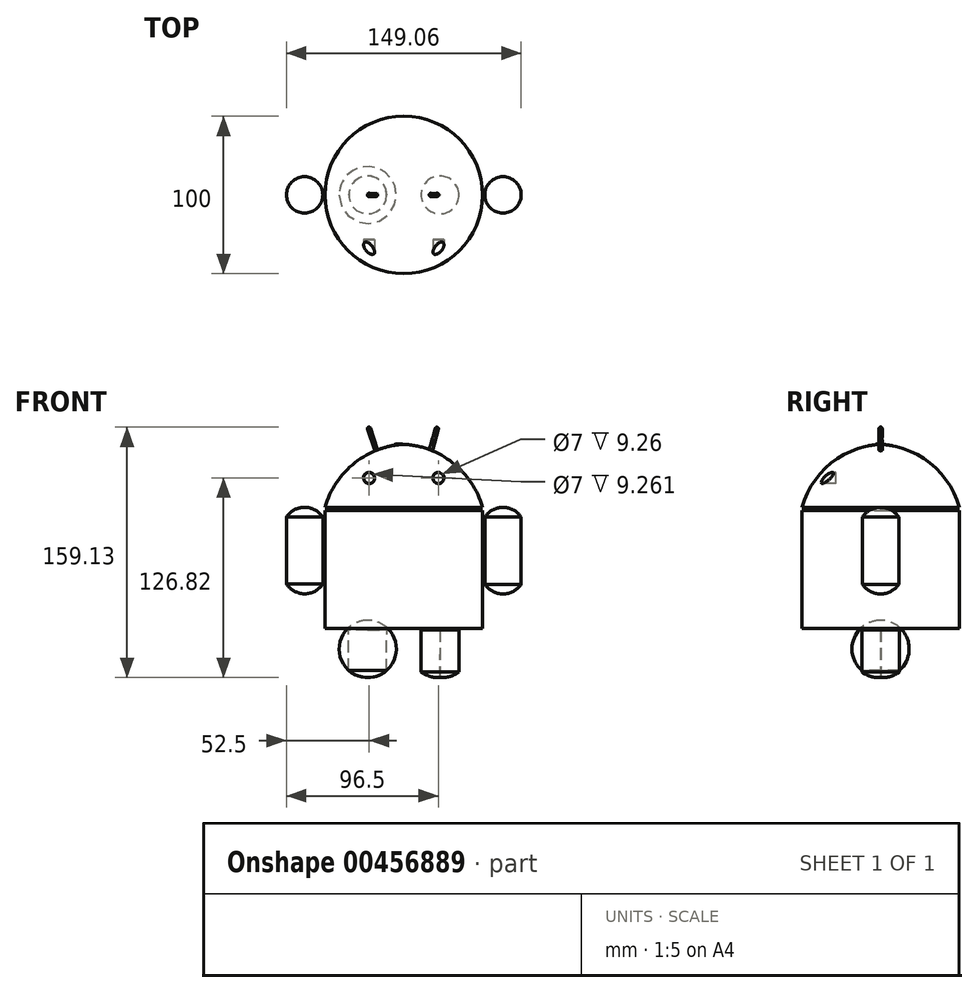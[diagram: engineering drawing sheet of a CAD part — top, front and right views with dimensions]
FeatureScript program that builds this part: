
annotation { "Feature Type Name" : "Feature", "Feature Type Description" : "" }
export const myFeature = defineFeature(function(context is Context, id is Id, definition is map)
    precondition{}
    {
        {
            var Q0;
            Q0=qCreatedBy(makeId("Front.planeOp"),FACE);
            var sketch = newSketch(context, id + "F0", { "sketchPlane" : qUnion([Q0])});
            skArc(sketch, "E0", {"start": v(0, 40) * mm, "mid": v(-31.42, 28.03) * mm, "end": v(-50, 0) * mm});
            skLineSegment(sketch, "E1", {"start": v(-50, 0) * mm, "end": v(0, 0) * mm});
            skLineSegment(sketch, "E2", {"start": v(0, 0) * mm, "end": v(0, 40) * mm});
            skSolve(sketch);
        }
        {
            var Q0;
            Q0=makeQuery(id+"F0.imprint","IMPRINT",FACE,{"disambiguationData":[TD([[makeQuery(id+"F0.imprint","IMPRINT",EDGE,{"derivedFrom":sQuery(id+"F0.wireOp",EDGE,"E0")}),1.0]])]});
            var Q1;
            Q1=sQuery(id+"F0.wireOp",EDGE,"E2");
            revolve(context, id + "F1", {"entities" : qUnion([Q0]), "axis" : qUnion([Q1]), "revolveType" : RevolveType.FULL});
        }
        {
            var Q0;
            Q0=qCreatedBy(makeId("Front.planeOp"),FACE);
            var sketch = newSketch(context, id + "F2", { "sketchPlane" : qUnion([Q0])});
            skLineSegment(sketch, "E3.bottom", {"start": v(0, -77) * mm, "end": v(-50, -77) * mm});
            skLineSegment(sketch, "E3.top", {"start": v(0, -2) * mm, "end": v(-50, -2) * mm});
            skLineSegment(sketch, "E3.left", {"start": v(0, -77) * mm, "end": v(0, -2) * mm});
            skLineSegment(sketch, "E3.right", {"start": v(-50, -77) * mm, "end": v(-50, -2) * mm});
            skSolve(sketch);
        }
        {
            var Q0;
            Q0=makeQuery(id+"F2.imprint","IMPRINT",FACE,{"disambiguationData":[TD([[makeQuery(id+"F2.imprint","IMPRINT",EDGE,{"derivedFrom":sQuery(id+"F2.wireOp",EDGE,"E3.bottom")}),-1.0]])]});
            var Q1;
            Q1=sQuery(id+"F2.wireOp",EDGE,"E3.left");
            revolve(context, id + "F3", {"entities" : qUnion([Q0]), "axis" : qUnion([Q1]), "revolveType" : RevolveType.FULL});
        }
        {
            var Q0;
            Q0=qCreatedBy(makeId("Front.planeOp"),FACE);
            cPlane(context, id + "F4", {"entities" : qUnion([Q0]), "cplaneType" : CPlaneType.OFFSET, "offset" : 38.5 * mm, "width" : 150 * mm, "height" : 150 * mm});
        }
        {
            var Q0;
            Q0=qCreatedBy(id+"F4.planeOp",FACE);
            var sketch = newSketch(context, id + "F5", { "sketchPlane" : qUnion([Q0])});
            skCircle(sketch, "E4", {"center": v(-22, 18.6) * mm, "radius": 3.5 * mm});
            skCircle(sketch, "E5", {"center": v(22, 18.6) * mm, "radius": 3.5 * mm});
            skSolve(sketch);
        }
        {
            var Q0;
            Q0 = qSketchRegion(id + "F5", true);
            extrude(context, id + "F6", {"entities" : qUnion([Q0]), "operationType" : NewBodyOperationType.REMOVE, "oppositeDirection" : true, "depth" : 10 * mm});
        }
        {
            var Q0;
            Q0=qCreatedBy(makeId("Front.planeOp"),FACE);
            var sketch = newSketch(context, id + "F7", { "sketchPlane" : qUnion([Q0])});
            skLineSegment(sketch, "E6", {"start": v(-15, 28.86) * mm, "end": v(-22.4, 50.82) * mm});
            skLineSegment(sketch, "E7", {"start": v(15, 29.08) * mm, "end": v(21.3, 50.82) * mm});
            skSolve(sketch);
        }
        {
            var Q0;
            Q0=qCreatedBy(makeId("Front.planeOp"),FACE);
            var sketch = newSketch(context, id + "F8", { "sketchPlane" : qUnion([Q0])});
            skArc(sketch, "E8", {"start": v(-22.43, 50.86) * mm, "mid": v(-23.02, 50.35) * mm, "end": v(-23.1, 49.57) * mm});
            skLineSegment(sketch, "E9", {"start": v(-23.1, 49.57) * mm, "end": v(-18.36, 35.82) * mm});
            skLineSegment(sketch, "E10", {"start": v(-18.36, 35.82) * mm, "end": v(-17.46, 36.13) * mm});
            skLineSegment(sketch, "E11", {"start": v(-17.46, 36.13) * mm, "end": v(-22.43, 50.86) * mm});
            skSolve(sketch);
        }
        {
            var Q0;
            Q0 = qSketchRegion(id + "F8", true);
            var Q1;
            Q1=sQuery(id+"F8.wireOp",EDGE,"E11");
            revolve(context, id + "F9", {"operationType" : NewBodyOperationType.ADD, "entities" : qUnion([Q0]), "axis" : qUnion([Q1]), "revolveType" : RevolveType.FULL});
        }
        {
            var Q0;
            Q0=qCreatedBy(makeId("Front.planeOp"),FACE);
            var sketch = newSketch(context, id + "F10", { "sketchPlane" : qUnion([Q0])});
            skArc(sketch, "E12", {"start": v(21.29, 50.83) * mm, "mid": v(20.67, 50.81) * mm, "end": v(20.16, 50.46) * mm});
            skLineSegment(sketch, "E13.0", {"start": v(14.04, 29.35) * mm, "end": v(20.16, 50.46) * mm});
            skLineSegment(sketch, "E14", {"start": v(14.04, 29.35) * mm, "end": v(15.08, 29.05) * mm});
            skLineSegment(sketch, "E15", {"start": v(15.08, 29.05) * mm, "end": v(21.29, 50.83) * mm});
            skSolve(sketch);
        }
        {
            var Q0;
            Q0=makeQuery(id+"F10.imprint","IMPRINT",FACE,{"disambiguationData":[TD([[makeQuery(id+"F10.imprint","IMPRINT",EDGE,{"derivedFrom":sQuery(id+"F10.wireOp",EDGE,"E12")}),1.0]])]});
            var Q1;
            Q1=sQuery(id+"F10.wireOp",EDGE,"E15");
            revolve(context, id + "F11", {"operationType" : NewBodyOperationType.ADD, "entities" : qUnion([Q0]), "axis" : qUnion([Q1]), "revolveType" : RevolveType.FULL});
        }
        {
            var Q0;
            Q0=qCreatedBy(makeId("Front.planeOp"),FACE);
            var sketch = newSketch(context, id + "F12", { "sketchPlane" : qUnion([Q0])});
            skArc(sketch, "E16", {"start": v(-62.96, 0) * mm, "mid": v(-69.5, -1.63) * mm, "end": v(-74.5, -6.15) * mm});
            skLineSegment(sketch, "E17", {"start": v(-74.5, -6.15) * mm, "end": v(-74.5, -48.81) * mm});
            skArc(sketch, "E18", {"start": v(-74.5, -48.81) * mm, "mid": v(-69.5, -53.33) * mm, "end": v(-62.96, -54.96) * mm});
            skLineSegment(sketch, "E19", {"start": v(-62.96, 0) * mm, "end": v(-62.96, -54.96) * mm});
            skLineSegment(sketch, "E20", {"start": v(-62.96, 0) * mm, "end": v(0, 0) * mm, "construction": true});
            skLineSegment(sketch, "E21", {"start": v(-62.96, -54.96) * mm, "end": v(0, 0) * mm, "construction": true});
            skSolve(sketch);
        }
        {
            var Q0;
            Q0=makeQuery(id+"F12.imprint","IMPRINT",FACE,{"disambiguationData":[TD([[makeQuery(id+"F12.imprint","IMPRINT",EDGE,{"derivedFrom":sQuery(id+"F12.wireOp",EDGE,"E16")}),1.0]])]});
            var Q1;
            Q1=sQuery(id+"F12.wireOp",EDGE,"E19");
            revolve(context, id + "F13", {"entities" : qUnion([Q0]), "axis" : qUnion([Q1]), "revolveType" : RevolveType.FULL});
        }
        {
            var Q0;
            Q0=qCreatedBy(makeId("Front.planeOp"),FACE);
            var sketch = newSketch(context, id + "F14", { "sketchPlane" : qUnion([Q0])});
            skArc(sketch, "E22", {"start": v(63.03, 0) * mm, "mid": v(56.47, -1.67) * mm, "end": v(51.49, -6.24) * mm});
            skLineSegment(sketch, "E23", {"start": v(51.49, -6.24) * mm, "end": v(51.49, -48.9) * mm});
            skArc(sketch, "E24", {"start": v(51.49, -48.9) * mm, "mid": v(56.49, -53.42) * mm, "end": v(63.03, -55.05) * mm});
            skLineSegment(sketch, "E25", {"start": v(63.03, 0) * mm, "end": v(63.03, -55.05) * mm});
            skLineSegment(sketch, "E26", {"start": v(0, 0) * mm, "end": v(63.03, 0) * mm, "construction": true});
            skLineSegment(sketch, "E27", {"start": v(0, 0) * mm, "end": v(63.03, -55.05) * mm, "construction": true});
            skLineSegment(sketch, "E28", {"start": v(51.49, -6.24) * mm, "end": v(0, 0) * mm, "construction": true});
            skSolve(sketch);
        }
        {
            var Q0;
            Q0=makeQuery(id+"F14.imprint","IMPRINT",FACE,{"disambiguationData":[TD([[makeQuery(id+"F14.imprint","IMPRINT",EDGE,{"derivedFrom":sQuery(id+"F14.wireOp",EDGE,"E22")}),1.0]])]});
            var Q1;
            Q1=sQuery(id+"F14.wireOp",EDGE,"E25");
            revolve(context, id + "F15", {"entities" : qUnion([Q0]), "axis" : qUnion([Q1]), "revolveType" : RevolveType.FULL});
        }
        {
            var Q0;
            Q0=qCreatedBy(makeId("Front.planeOp"),FACE);
            var sketch = newSketch(context, id + "F16", { "sketchPlane" : qUnion([Q0])});
            skLineSegment(sketch, "E29", {"start": v(-23, -78) * mm, "end": v(-23, -108) * mm});
            skLineSegment(sketch, "E30", {"start": v(23, -78) * mm, "end": v(23, -108) * mm});
            skSolve(sketch);
        }
        {
            var Q0;
            Q0=qCreatedBy(makeId("Front.planeOp"),FACE);
            var sketch = newSketch(context, id + "F17", { "sketchPlane" : qUnion([Q0])});
            skArc(sketch, "E31", {"start": v(-34.97, -103.67) * mm, "mid": v(-29.36, -107.02) * mm, "end": v(-22.93, -108.18) * mm});
            skLineSegment(sketch, "E32", {"start": v(-34.97, -103.67) * mm, "end": v(-34.97, -78) * mm});
            skLineSegment(sketch, "E33", {"start": v(-34.97, -78) * mm, "end": v(-22.86, -78) * mm});
            skLineSegment(sketch, "E34", {"start": v(-22.86, -78) * mm, "end": v(-22.93, -108.18) * mm});
            skSolve(sketch);
        }
        {
            var Q0;
            Q0=qCreatedBy(makeId("Front.planeOp"),FACE);
            var sketch = newSketch(context, id + "F18", { "sketchPlane" : qUnion([Q0])});
            skLineSegment(sketch, "E35", {"start": v(11, -78) * mm, "end": v(11, -104.6) * mm});
            skArc(sketch, "E36", {"start": v(11, -104.6) * mm, "mid": v(16.6, -107.43) * mm, "end": v(22.82, -108.2) * mm});
            skLineSegment(sketch, "E37", {"start": v(11, -78) * mm, "end": v(22.9, -78) * mm});
            skLineSegment(sketch, "E38", {"start": v(22.9, -78) * mm, "end": v(22.82, -108.2) * mm});
            skSolve(sketch);
        }
        {
            var Q0;
            Q0 = qSketchRegion(id + "F17", true);
            var Q1;
            Q1=sQuery(id+"F17.wireOp",EDGE,"E34");
            revolve(context, id + "F19", {"entities" : qUnion([Q0]), "axis" : qUnion([Q1]), "revolveType" : RevolveType.FULL});
        }
        {
            var Q0;
            Q0 = qSketchRegion(id + "F18", true);
            var Q1;
            Q1=sQuery(id+"F16.wireOp",EDGE,"E30");
            revolve(context, id + "F20", {"entities" : qUnion([Q0]), "axis" : qUnion([Q1]), "revolveType" : RevolveType.FULL});
        }
    });
